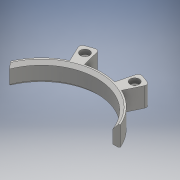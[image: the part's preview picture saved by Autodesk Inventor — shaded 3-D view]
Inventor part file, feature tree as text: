
AUTODESK INVENTOR PART (.ipt)
format: ipt  version: 2016 (Build 200138000, 138)  size: 192,512 bytes
history: native  units: mm
features: reference x6, hole x2, chamfer x2, other x1, extrude x1, sketch x1, fillet x1
ambient origin geometry x8: Origin, YZ Plane, XZ Plane, XY Plane, X Axis, Y Axis, Z Axis, Center Point
bodies: Solid1 (feature_tree)
feature tree (14):
  other  "Transmission.ipt"
  extrude  "Extrusion1"  Depth=10.0mm
  sketch  "Sketch2"  dims[d0=72.0mm d2=10.0mm d5=42.92mm d3=42.92mm d4=42.92mm d6=3.0mm d7=3.0mm d8=12.7mm d9=0.0mm d10=3.1mm d11=6.0mm d12=4.0mm d13=2.0mm d14=90.0deg d15=8.0mm d16=20.594885mm d17=2.0mm d18=2.0mm d19=45.0deg d20=2.0mm d21=2.0mm d22=45.0deg d23=6.0mm d24=6.0mm d25=4.0mm d26=2.0mm d27=90.0deg d28=3.0mm d29=0.0mm d33=3.0mm d34=4.5mm d35=4.5mm d36=4.5mm d37=4.5mm d38=2.0mm]
  hole  "Hole1"  [1 undecoded]
  hole  "Hole2"  [1 undecoded]
  chamfer  "Chamfer1"  Distance=42.92mm
  chamfer  "Chamfer2"  Distance=3.0mm
  fillet  "Fillet1"  Radius=3.0mm
  reference  "Reference1"
  reference  "Reference2"
  reference  "Reference3"
  reference  "Reference4"
  reference  "Reference5"
  reference  "Reference6"
note: 2 required parameter values undecoded (feature->parameter linkage not recoverable at this tier; creation-order binding heuristic only, values carry confidence <= 0.55)
